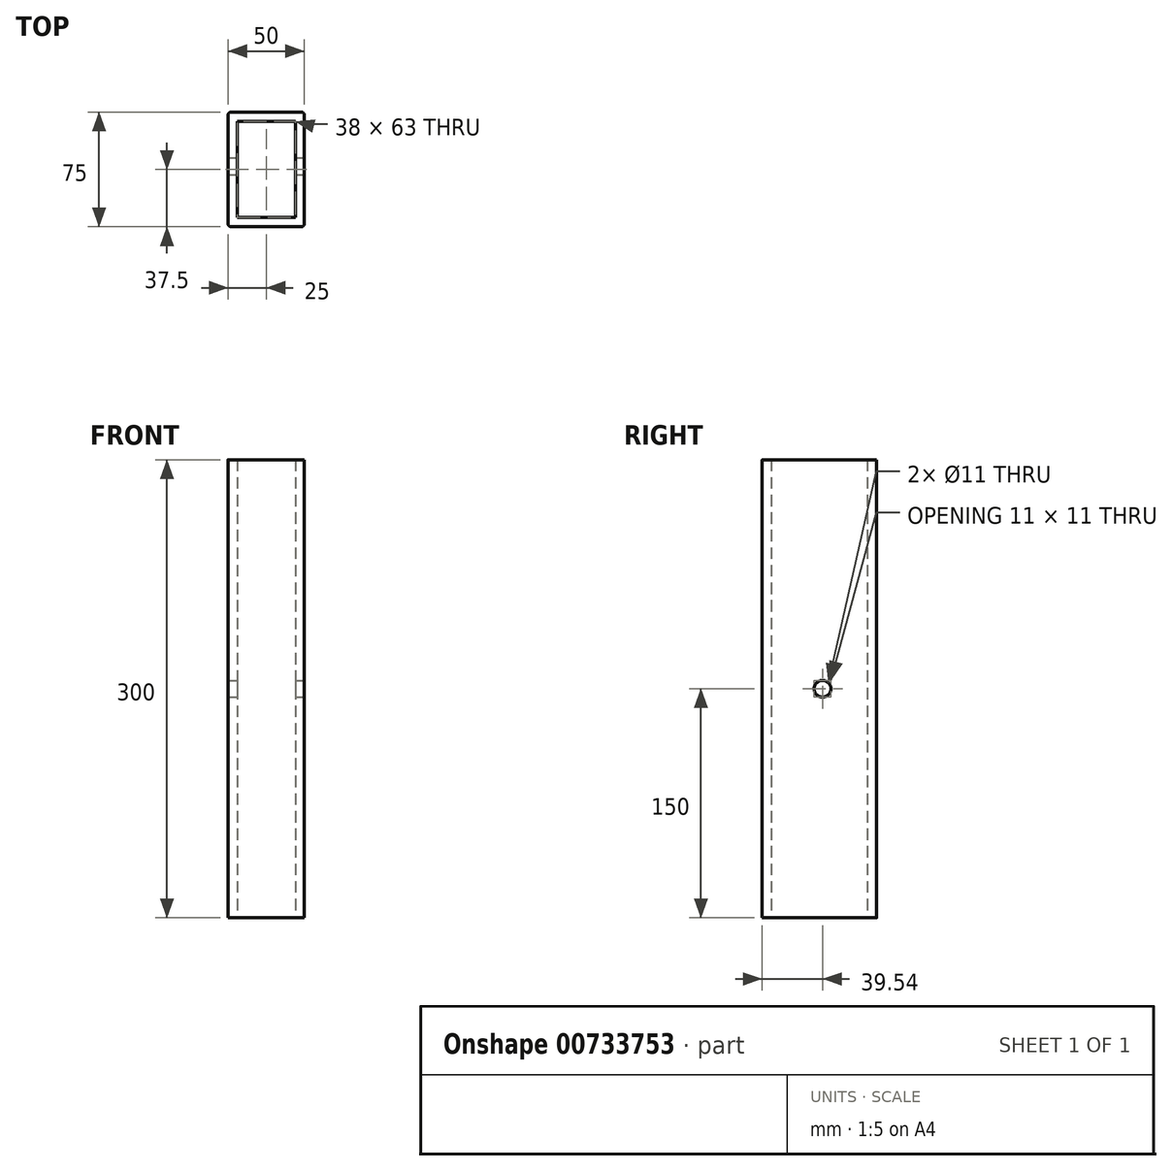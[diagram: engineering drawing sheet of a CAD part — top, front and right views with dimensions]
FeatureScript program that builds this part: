
annotation { "Feature Type Name" : "Feature", "Feature Type Description" : "" }
export const myFeature = defineFeature(function(context is Context, id is Id, definition is map)
    precondition{}
    {
        {
            var Q0;
            Q0=qCreatedBy(makeId("Top.planeOp"),FACE);
            var sketch = newSketch(context, id + "F0", { "sketchPlane" : qUnion([Q0])});
            skLineSegment(sketch, "E0.bottom", {"start": v(23, -37.5) * mm, "end": v(-23, -37.5) * mm});
            skLineSegment(sketch, "E0.top", {"start": v(23, 37.5) * mm, "end": v(-23, 37.5) * mm});
            skLineSegment(sketch, "E0.left", {"start": v(25, -35.5) * mm, "end": v(25, 35.5) * mm});
            skLineSegment(sketch, "E0.right", {"start": v(-25, -35.5) * mm, "end": v(-25, 35.5) * mm});
            skPoint(sketch, "E0.middle", {"position": v(0, 0) * mm});
            skPoint(sketch, "E1.visualSharp", {"position": v(25, -37.5) * mm});
            skArc(sketch, "E1.filletArc", {"start": v(23, -37.5) * mm, "mid": v(24.41, -36.91) * mm, "end": v(25, -35.5) * mm});
            skPoint(sketch, "E2.visualSharp", {"position": v(25, 37.5) * mm});
            skArc(sketch, "E2.filletArc", {"start": v(25, 35.5) * mm, "mid": v(24.41, 36.91) * mm, "end": v(23, 37.5) * mm});
            skPoint(sketch, "E3.visualSharp", {"position": v(-25, 37.5) * mm});
            skArc(sketch, "E3.filletArc", {"start": v(-23, 37.5) * mm, "mid": v(-24.41, 36.91) * mm, "end": v(-25, 35.5) * mm});
            skPoint(sketch, "E4.visualSharp", {"position": v(-25, -37.5) * mm});
            skArc(sketch, "E4.filletArc", {"start": v(-25, -35.5) * mm, "mid": v(-24.41, -36.91) * mm, "end": v(-23, -37.5) * mm});
            skLineSegment(sketch, "E5.0", {"start": v(19, -31.5) * mm, "end": v(19, 31.5) * mm});
            skLineSegment(sketch, "E5.1", {"start": v(19, -31.5) * mm, "end": v(-19, -31.5) * mm});
            skLineSegment(sketch, "E5.2", {"start": v(-19, -31.5) * mm, "end": v(-19, 31.5) * mm});
            skLineSegment(sketch, "E5.3", {"start": v(19, 31.5) * mm, "end": v(-19, 31.5) * mm});
            skSolve(sketch);
        }
        {
            var Q0;
            Q0=makeQuery(id+"F0.imprint","IMPRINT",FACE,{"disambiguationData":[TD([[makeQuery(id+"F0.imprint","IMPRINT",EDGE,{"derivedFrom":sQuery(id+"F0.wireOp",EDGE,"E0.bottom")}),-1.0]])]});
            extrude(context, id + "F1", {"entities" : qUnion([Q0]), "depth" : 300 * mm, "offsetDistance" : 25 * mm});
        }
        {
            var Q0;
            Q0=makeQuery(id+"F1.opExtrude","SWEPT_FACE",FACE,{"disambiguationData":[OSD([sQuery(id+"F0.wireOp",EDGE,"E0.left")])]});
            var sketch = newSketch(context, id + "F2", { "sketchPlane" : qUnion([Q0])});
            skLineSegment(sketch, "E6", {"start": v(2.04, 0) * mm, "end": v(2.04, 150) * mm});
            skCircle(sketch, "E7", {"center": v(2.04, 150) * mm, "radius": 5.5 * mm});
            skSolve(sketch);
        }
        {
            var Q0;
            Q0=makeQuery(id+"F2.imprint","IMPRINT",FACE,{"disambiguationData":[TD([[makeQuery(id+"F2.imprint","IMPRINT",EDGE,{"derivedFrom":sQuery(id+"F2.wireOp",EDGE,"E7")}),1.0]])]});
            extrude(context, id + "F3", {"entities" : qUnion([Q0]), "operationType" : NewBodyOperationType.REMOVE, "oppositeDirection" : true, "depth" : 50 * mm, "offsetDistance" : 25 * mm});
        }
    });
